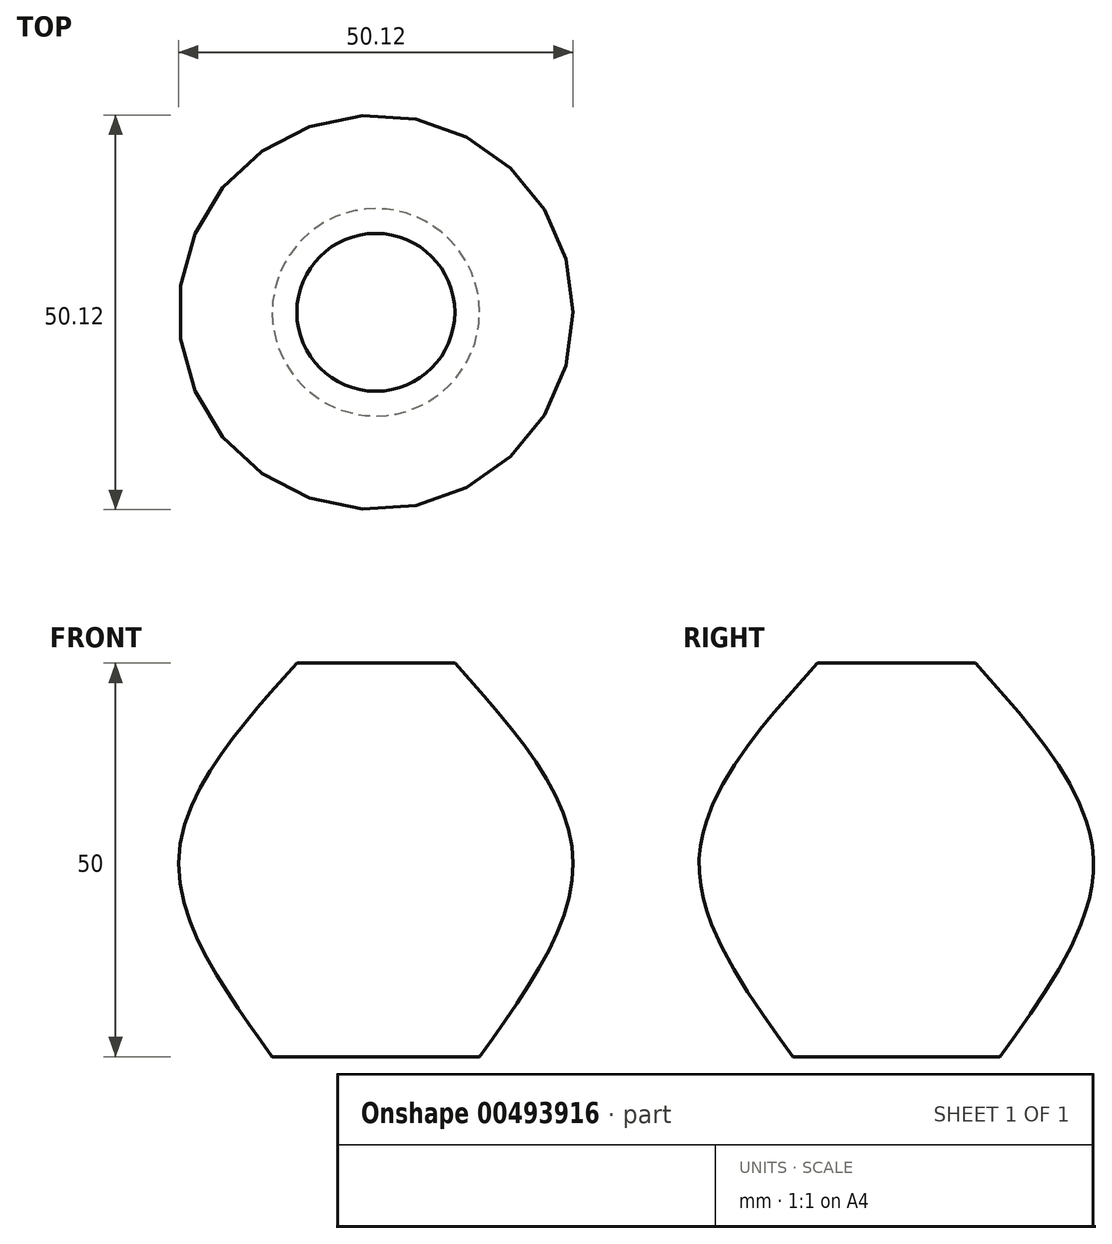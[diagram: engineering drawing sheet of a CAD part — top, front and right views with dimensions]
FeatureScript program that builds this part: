
annotation { "Feature Type Name" : "Feature", "Feature Type Description" : "" }
export const myFeature = defineFeature(function(context is Context, id is Id, definition is map)
    precondition{}
    {
        {
            var Q0;
            Q0=qCreatedBy(makeId("Top.planeOp"),FACE);
            cPlane(context, id + "F0", {"entities" : qUnion([Q0]), "cplaneType" : CPlaneType.OFFSET, "offset" : 25 * mm, "width" : 150 * mm, "height" : 150 * mm});
        }
        {
            var Q0;
            Q0=qCreatedBy(id+"F0.planeOp",FACE);
            cPlane(context, id + "F1", {"entities" : qUnion([Q0]), "cplaneType" : CPlaneType.OFFSET, "offset" : 25 * mm, "width" : 150 * mm, "height" : 150 * mm});
        }
        {
            var Q0;
            Q0=qCreatedBy(makeId("Top.planeOp"),FACE);
            var sketch = newSketch(context, id + "F2", { "sketchPlane" : qUnion([Q0])});
            skCircle(sketch, "E0", {"center": v(0, 0) * mm, "radius": 13.16 * mm});
            skSolve(sketch);
        }
        {
            var Q0;
            Q0=qCreatedBy(id+"F0.planeOp",FACE);
            var sketch = newSketch(context, id + "F3", { "sketchPlane" : qUnion([Q0])});
            skCircle(sketch, "E1", {"center": v(0, 0) * mm, "radius": 25.05 * mm});
            skSolve(sketch);
        }
        {
            var Q0;
            Q0=qCreatedBy(id+"F1.planeOp",FACE);
            var sketch = newSketch(context, id + "F4", { "sketchPlane" : qUnion([Q0])});
            skCircle(sketch, "E2", {"center": v(0, 0) * mm, "radius": 10.03 * mm});
            skSolve(sketch);
        }
        {
            var Q0;
            Q0=makeQuery(id+"F2.imprint","IMPRINT",FACE,{"disambiguationData":[TD([[makeQuery(id+"F2.imprint","IMPRINT",EDGE,{"derivedFrom":sQuery(id+"F2.wireOp",EDGE,"E0")}),1.0]])]});
            var Q1;
            Q1=makeQuery(id+"F3.imprint","IMPRINT",FACE,{"disambiguationData":[TD([[makeQuery(id+"F3.imprint","IMPRINT",EDGE,{"derivedFrom":sQuery(id+"F3.wireOp",EDGE,"E1")}),1.0]])]});
            var Q2;
            Q2=makeQuery(id+"F4.imprint","IMPRINT",FACE,{"disambiguationData":[TD([[makeQuery(id+"F4.imprint","IMPRINT",EDGE,{"derivedFrom":sQuery(id+"F4.wireOp",EDGE,"E2")}),1.0]])]});
            loft(context, id + "F5", {"sheetProfilesArray" : [{ "sheetProfileEntities" : qUnion([Q0]) }, { "sheetProfileEntities" : qUnion([Q1]) }, { "sheetProfileEntities" : qUnion([Q2]) }]});
        }
    });
